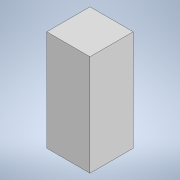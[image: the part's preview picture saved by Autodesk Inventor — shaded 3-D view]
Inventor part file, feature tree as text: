
AUTODESK INVENTOR PART (.ipt)
format: ipt  version: 2022 (Build 260153000, 153)  size: 89,600 bytes
history: native  units: mm
features: extrude x1, sketch x1
ambient origin geometry x8: Origin, YZ Plane, XZ Plane, XY Plane, X Axis, Y Axis, Z Axis, Center Point
bodies: Body1 (feature_tree)
feature tree (2):
  extrude  "Extrusion7"  Depth=30.0mm
  sketch  "Sketch8"  dims[d18=30.0mm d19=30.0mm d22=70.0mm d23=0.0mm]
